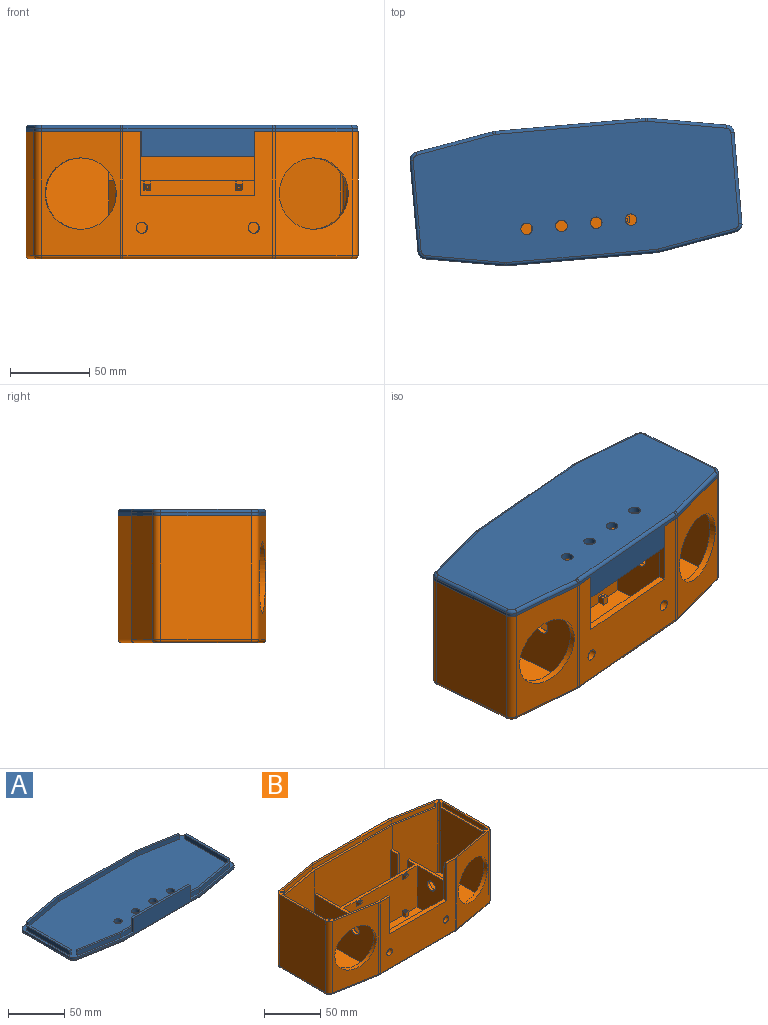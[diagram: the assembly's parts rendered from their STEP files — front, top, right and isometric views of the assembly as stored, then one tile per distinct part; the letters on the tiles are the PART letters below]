
ASSEMBLY  parts=2 mates=1
PART A: 71 faces, bbox 205.8x85.1x19.9 mm
  f0: plane 205x85mm, normal (0,0,1), area 15053.5mm2, adj f1,f2,f3,f4,f5,f6,f7,f8
  f1: plane 13.31x5mm, normal (0,-1,0), area 66.5mm2, adj f0,f49,f52,f64
  f2: plane 49.24x8.68mm, normal (-0.17,0.98,0), area 100mm2, adj f0,f3,f17,f27
  f3: cylinder r=5mm len=4.92mm, axis (0,0,1), area 14mm2, adj f0,f2,f4,f25
  f4: plane 57.48x2mm, normal (-1,0,0), area 115mm2, adj f0,f3,f5,f23
  f5: cylinder r=5mm len=4.92mm, axis (0,0,1), area 14mm2, adj f0,f4,f6,f21
  f6: plane 49.24x8.68mm, normal (-0.17,-0.98,0), area 100mm2, adj f0,f5,f7,f19
  f7: cylinder r=10mm len=2mm, axis (0,0,1), area 3.5mm2, adj f0,f6,f8,f20
  f8: plane 94.78x17.9mm, normal (0,-1,0), area 1332.8mm2, adj f0,f7,f9,f22,f64,f65,f66
  f9: cylinder r=10mm len=2mm, axis (0,0,1), area 3.5mm2, adj f0,f8,f10,f24
  f10: plane 49.24x8.68mm, normal (0.17,-0.98,0), area 100mm2, adj f0,f9,f11,f26
  f11: cylinder r=5mm len=4.92mm, axis (0,0,1), area 14mm2, adj f0,f10,f12,f28
  f12: plane 57.48x2mm, normal (1,0,0), area 115mm2, adj f0,f11,f13,f30
  f13: cylinder r=5mm len=4.92mm, axis (0,0,1), area 14mm2, adj f0,f12,f14,f32
  f14: plane 49.24x8.68mm, normal (0.17,0.98,0), area 100mm2, adj f0,f13,f15,f34
  f15: cylinder r=10mm len=2mm, axis (0,0,1), area 3.5mm2, adj f0,f14,f16,f33
  f16: plane 94.78x2mm, normal (0,1,0), area 189.6mm2, adj f0,f15,f17,f31
  f17: cylinder r=10mm len=2mm, axis (0,0,1), area 3.5mm2, adj f0,f2,f16,f29
  f18: plane 201x81mm, normal (0,0,-1), area 15139.7mm2, adj f19,f20,f21,f22,f23,f24,f25,f26
  f19: cylinder r=2mm len=49.59mm, axis (-0.98,0.17,0), area 157.1mm2, adj f6,f18,f20,f21
  f20: torus R=8mm, axis (0,0,1), area 5.1mm2, adj f7,f18,f19,f22
  f21: torus R=3mm, axis (0,0,1), area 18.7mm2, adj f5,f18,f19,f23
  f22: cylinder r=2mm len=94.78mm, axis (-1,0,0), area 297.8mm2, adj f8,f18,f20,f24
  f23: cylinder r=2mm len=57.48mm, axis (0,1,0), area 180.6mm2, adj f4,f18,f21,f25
  f24: torus R=8mm, axis (0,0,1), area 5.1mm2, adj f9,f18,f22,f26
  f25: torus R=3mm, axis (0,0,1), area 18.7mm2, adj f3,f18,f23,f27
  f26: cylinder r=2mm len=49.59mm, axis (-0.98,-0.17,0), area 157.1mm2, adj f10,f18,f24,f28
  f27: cylinder r=2mm len=49.59mm, axis (0.98,0.17,0), area 157.1mm2, adj f2,f18,f25,f29
  f28: torus R=3mm, axis (0,0,1), area 18.7mm2, adj f11,f18,f26,f30
  f29: torus R=8mm, axis (0,0,1), area 5.1mm2, adj f17,f18,f27,f31
  f30: cylinder r=2mm len=57.48mm, axis (0,-1,0), area 180.6mm2, adj f12,f18,f28,f32
  f31: cylinder r=2mm len=94.78mm, axis (1,0,0), area 297.8mm2, adj f16,f18,f29,f33
  f32: torus R=3mm, axis (0,0,1), area 18.7mm2, adj f13,f18,f30,f34
  f33: torus R=8mm, axis (0,0,1), area 5.1mm2, adj f15,f18,f31,f34
  f34: cylinder r=2mm len=49.59mm, axis (0.98,-0.17,0), area 157.1mm2, adj f14,f18,f32,f33
  f35: plane 46.56x8.21mm, normal (0.17,0.98,0), area 236.4mm2, adj f0,f36,f42,f43
  f36: plane 98.52x5mm, normal (0,1,0), area 492.6mm2, adj f0,f35,f37,f43
  f37: plane 46.56x8.21mm, normal (-0.17,0.98,0), area 236.4mm2, adj f0,f36,f38,f43
  f38: plane 5x1.97mm, normal (-0.98,-0.17,0), area 10mm2, adj f0,f37,f39,f43
  f39: plane 46.22x8.15mm, normal (0.17,-0.98,0), area 234.7mm2, adj f0,f38,f40,f43
  f40: plane 98.52x5mm, normal (0,-1,0), area 492.6mm2, adj f0,f39,f41,f43
  f41: plane 46.22x8.15mm, normal (-0.17,-0.98,0), area 234.7mm2, adj f0,f40,f42,f43
  f42: plane 5x1.97mm, normal (0.98,-0.17,0), area 10mm2, adj f0,f35,f41,f43
  f43: plane 191.65x10.18mm, normal (0,0,1), area 388.5mm2, adj f35,f36,f37,f38,f39,f40,f41,f42
  f44: plane 98.52x5mm, normal (0,1,0), area 492.6mm2, adj f0,f45,f51,f52
  f45: plane 46.22x8.15mm, normal (0.17,0.98,0), area 234.7mm2, adj f0,f44,f46,f52
  f46: plane 5x1.97mm, normal (-0.98,0.17,0), area 10mm2, adj f0,f45,f47,f52
  f47: plane 46.56x8.21mm, normal (-0.17,-0.98,0), area 236.4mm2, adj f0,f46,f48,f52
  f48: plane 13.31x5mm, normal (0,-1,0), area 66.5mm2, adj f0,f47,f52,f65
  f49: plane 46.56x8.21mm, normal (0.17,-0.98,0), area 236.4mm2, adj f0,f1,f50,f52
  f50: plane 5x1.97mm, normal (0.98,0.17,0), area 10mm2, adj f0,f49,f51,f52
  f51: plane 46.22x8.15mm, normal (-0.17,0.98,0), area 234.7mm2, adj f0,f44,f50,f52
  f52: plane 191.65x10.18mm, normal (0,0,1), area 388.5mm2, adj f1,f44,f45,f46,f47,f48,f49,f50
  f53: plane 54.21x5mm, normal (-1,0,0), area 271.1mm2, adj f0,f54,f56,f57
  f54: plane 5x2mm, normal (0,-1,0), area 10mm2, adj f0,f53,f55,f57
  f55: plane 54.21x5mm, normal (1,0,0), area 271.1mm2, adj f0,f54,f56,f57
  f56: plane 5x2mm, normal (0,1,0), area 10mm2, adj f0,f53,f55,f57
  f57: plane 54.21x2mm, normal (0,0,1), area 108.4mm2, adj f53,f54,f55,f56
  f58: plane 54.21x5mm, normal (1,0,0), area 271.1mm2, adj f0,f59,f61,f62
  f59: plane 5x2mm, normal (0,1,0), area 10mm2, adj f0,f58,f60,f62
  f60: plane 54.21x5mm, normal (-1,0,0), area 271.1mm2, adj f0,f59,f61,f62
  f61: plane 5x2mm, normal (0,-1,0), area 10mm2, adj f0,f58,f60,f62
  f62: plane 54.21x2mm, normal (0,0,1), area 108.4mm2, adj f58,f59,f60,f61
  f63: plane 71.9x10.9mm, normal (0,1,0), area 783.7mm2, adj f52,f64,f65,f66
  f64: plane 15.9x2.21mm, normal (1,0,0), area 35.1mm2, adj f0,f1,f8,f63,f66
  f65: plane 15.9x2.21mm, normal (-1,0,0), area 35.1mm2, adj f0,f8,f48,f63,f66
  f66: plane 71.9x2.21mm, normal (0,0,1), area 158.6mm2, adj f8,f63,f64,f65
  f67: cylinder r=3.65mm len=7.3mm, axis (0,0,-1), area 91.7mm2, adj f0,f18
  f68: cylinder r=3.65mm len=7.3mm, axis (0,0,-1), area 91.7mm2, adj f0,f18
  f69: cylinder r=3.65mm len=7.3mm, axis (0,0,-1), area 91.7mm2, adj f0,f18
  f70: cylinder r=3.65mm len=7.3mm, axis (0,0,-1), area 91.7mm2, adj f0,f18
PART B: 147 faces, bbox 206.2x85.4x80.4 mm
  f0: plane 76x47.59mm, normal (-0.17,0.98,0), area 1843.8mm2, adj f2,f3,f6,f10,f51,f55,f83,f136
  f1: plane 76x47.59mm, normal (0.17,0.98,0), area 1843.8mm2, adj f2,f3,f12,f50,f56,f79,f84,f135
  f2: plane 205x85mm, normal (0,0,1), area 995.4mm2, adj f0,f1,f4,f5,f9,f14,f15,f16
  f3: plane 98.52x71mm, normal (0,1,0), area 4091.9mm2, adj f0,f1,f6,f8,f53,f54,f57,f84
  f4: plane 94.78x78mm, normal (0,-1,0), area 4400.1mm2, adj f2,f19,f20,f33,f130,f131,f132,f133
  f5: plane 13.26x5mm, normal (0,1,0), area 66.3mm2, adj f2,f6,f82,f131
  f6: plane 59.82x10.18mm, normal (0,0,1), area 121.1mm2, adj f0,f3,f5,f82,f83,f131
  f7: plane 92.52x45mm, normal (0,-1,0), area 4075.4mm2, adj f8,f53,f54,f57,f95,f97,f98,f99
  f8: plane 92.52x43mm, normal (0,0,1), area 3914.3mm2, adj f3,f7,f53,f54,f95,f96,f97,f99
  f9: plane 76x47.59mm, normal (0.17,-0.98,0), area 3437.8mm2, adj f2,f12,f13,f49,f56,f77,f78
  f10: plane 145.26x76.53mm, normal (0,0,1), area 6216.6mm2, adj f0,f11,f13,f47,f48,f51,f52,f55
  f11: plane 93.02x45mm, normal (0,1,0), area 4185.9mm2, adj f10,f57,f58,f60
  f12: plane 76.53x49.24mm, normal (0,0,1), area 3339.4mm2, adj f1,f9,f46,f49,f50,f56
  f13: plane 98.52x71mm, normal (0,-1,0), area 6747.4mm2, adj f9,f10,f48,f57,f58,f62,f64,f78
  f14: plane 78x49.24mm, normal (-0.17,0.98,0), area 3900mm2, adj f2,f15,f28,f38
  f15: cylinder r=5mm len=78mm, axis (0,0,1), area 544.5mm2, adj f2,f14,f16,f36
  f16: plane 78x57.48mm, normal (-1,0,0), area 4483.5mm2, adj f2,f15,f17,f34
  f17: cylinder r=5mm len=78mm, axis (0,0,1), area 544.5mm2, adj f2,f16,f18,f32
  f18: plane 78x49.24mm, normal (-0.17,-0.98,0), area 2309.6mm2, adj f2,f17,f19,f30,f135
  f19: cylinder r=10mm len=78mm, axis (0,0,1), area 136.2mm2, adj f2,f4,f18,f31
  f20: cylinder r=10mm len=78mm, axis (0,0,1), area 136.2mm2, adj f2,f4,f21,f35
  f21: plane 78x49.24mm, normal (0.17,-0.98,0), area 2309.6mm2, adj f2,f20,f22,f37,f136
  f22: cylinder r=5mm len=78mm, axis (0,0,1), area 544.5mm2, adj f2,f21,f23,f39
  f23: plane 78x57.48mm, normal (1,0,0), area 4483.5mm2, adj f2,f22,f24,f41
  f24: cylinder r=5mm len=78mm, axis (0,0,1), area 544.5mm2, adj f2,f23,f25,f43
  f25: plane 78x49.24mm, normal (0.17,0.98,0), area 3821.5mm2, adj f2,f24,f26,f45,f145
  f26: cylinder r=10mm len=78mm, axis (0,0,1), area 136.2mm2, adj f2,f25,f27,f44
  f27: plane 94.78x78mm, normal (0,1,0), area 7393.1mm2, adj f2,f26,f28,f42
  f28: cylinder r=10mm len=78mm, axis (0,0,1), area 136.2mm2, adj f2,f14,f27,f40
  f29: plane 201x81mm, normal (0,0,-1), area 15307.1mm2, adj f30,f31,f32,f33,f34,f35,f36,f37
  f30: cylinder r=2mm len=49.59mm, axis (-0.98,0.17,0), area 157.1mm2, adj f18,f29,f31,f32
  f31: torus R=8mm, axis (0,0,1), area 5.1mm2, adj f19,f29,f30,f33
  f32: torus R=3mm, axis (0,0,1), area 18.7mm2, adj f17,f29,f30,f34
  f33: cylinder r=2mm len=94.78mm, axis (-1,0,0), area 297.8mm2, adj f4,f29,f31,f35
  f34: cylinder r=2mm len=57.48mm, axis (0,1,0), area 180.6mm2, adj f16,f29,f32,f36
  f35: torus R=8mm, axis (0,0,1), area 5.1mm2, adj f20,f29,f33,f37
  f36: torus R=3mm, axis (0,0,1), area 18.7mm2, adj f15,f29,f34,f38
  f37: cylinder r=2mm len=49.59mm, axis (-0.98,-0.17,0), area 157.1mm2, adj f21,f29,f35,f39
  f38: cylinder r=2mm len=49.59mm, axis (0.98,0.17,0), area 157.1mm2, adj f14,f29,f36,f40
  f39: torus R=3mm, axis (0,0,1), area 18.7mm2, adj f22,f29,f37,f41
  f40: torus R=8mm, axis (0,0,1), area 5.1mm2, adj f28,f29,f38,f42
  f41: cylinder r=2mm len=57.48mm, axis (0,-1,0), area 180.6mm2, adj f23,f29,f39,f43
  f42: cylinder r=2mm len=94.78mm, axis (1,0,0), area 297.8mm2, adj f27,f29,f40,f44
  f43: torus R=3mm, axis (0,0,1), area 18.7mm2, adj f24,f29,f41,f45
  f44: torus R=8mm, axis (0,0,1), area 5.1mm2, adj f26,f29,f42,f45
  f45: cylinder r=2mm len=49.59mm, axis (0.98,-0.17,0), area 157.1mm2, adj f25,f29,f43,f44
  f46: plane 76x55.8mm, normal (1,0,0), area 3969.9mm2, adj f2,f12,f49,f50,f70,f71,f72
  f47: plane 76x55.8mm, normal (-1,0,0), area 3969.9mm2, adj f2,f10,f51,f52,f65,f67,f68
  f48: plane 76x47.59mm, normal (-0.17,-0.98,0), area 3359.3mm2, adj f2,f10,f13,f52,f61,f73,f78,f145
  f49: cylinder r=2mm len=76mm, axis (0,0,1), area 212.2mm2, adj f2,f9,f12,f46
  f50: cylinder r=2mm len=76mm, axis (0,0,-1), area 212.2mm2, adj f1,f2,f12,f46
  f51: cylinder r=2mm len=76mm, axis (0,0,1), area 212.2mm2, adj f0,f2,f10,f47
  f52: cylinder r=2mm len=76mm, axis (0,0,-1), area 212.2mm2, adj f2,f10,f47,f48
  f53: plane 45x43mm, normal (1,0,0), area 1856.5mm2, adj f3,f7,f8,f57,f93
  f54: plane 45x43mm, normal (-1,0,0), area 1856.5mm2, adj f3,f7,f8,f57,f94
  f55: plane 55x45mm, normal (1,0,0), area 2396.5mm2, adj f0,f10,f57,f59,f94
  f56: plane 76.53x45mm, normal (-1,0,0), area 3365.1mm2, adj f1,f9,f12,f57,f93
  f57: plane 98.52x76.53mm, normal (0,0,1), area 684.3mm2, adj f3,f7,f11,f13,f53,f54,f55,f56
  f58: plane 45x30.53mm, normal (1,0,0), area 1373.7mm2, adj f10,f11,f13,f57
  f59: plane 45x3mm, normal (0,1,0), area 135mm2, adj f10,f55,f57,f60
  f60: plane 45x9mm, normal (-1,0,0), area 405mm2, adj f10,f11,f57,f59
  f61: plane 45x9mm, normal (1,0,0), area 405mm2, adj f10,f48,f63,f64
  f62: plane 45x9mm, normal (-1,0,0), area 405mm2, adj f10,f13,f63,f64
  f63: plane 45x3mm, normal (0,-1,0), area 135mm2, adj f10,f61,f62,f64
  f64: plane 9x3mm, normal (0,0,1), area 27mm2, adj f13,f61,f62,f63
  f65: plane 5x2mm, normal (0,1,0), area 10mm2, adj f2,f47,f66,f68
  f66: plane 54.21x5mm, normal (-1,0,0), area 271.1mm2, adj f2,f65,f67,f68
  f67: plane 5x2mm, normal (0,-1,0), area 10mm2, adj f2,f47,f66,f68
  f68: plane 54.21x2mm, normal (0,0,1), area 108.4mm2, adj f47,f65,f66,f67
  f69: plane 54.21x5mm, normal (1,0,0), area 271.1mm2, adj f2,f70,f71,f72
  f70: plane 5x2mm, normal (0,1,0), area 10mm2, adj f2,f46,f69,f72
  f71: plane 5x2mm, normal (0,-1,0), area 10mm2, adj f2,f46,f69,f72
  f72: plane 54.21x2mm, normal (0,0,1), area 108.4mm2, adj f46,f69,f70,f71
  f73: plane 5x1.97mm, normal (-0.98,0.17,0), area 10mm2, adj f2,f48,f74,f78
  f74: plane 46.56x8.21mm, normal (-0.17,-0.98,0), area 236.4mm2, adj f2,f73,f75,f78
  f75: plane 98.52x5mm, normal (0,-1,0), area 492.6mm2, adj f2,f74,f76,f78
  f76: plane 46.56x8.21mm, normal (0.17,-0.98,0), area 236.4mm2, adj f2,f75,f77,f78
  f77: plane 5x1.97mm, normal (0.98,0.17,0), area 10mm2, adj f2,f9,f76,f78
  f78: plane 191.65x10.18mm, normal (0,0,1), area 388.5mm2, adj f9,f13,f48,f73,f74,f75,f76,f77
  f79: plane 5x1.97mm, normal (0.98,-0.17,0), area 10mm2, adj f1,f2,f80,f84
  f80: plane 46.56x8.21mm, normal (0.17,0.98,0), area 236.4mm2, adj f2,f79,f81,f84
  f81: plane 13.26x5mm, normal (0,1,0), area 66.3mm2, adj f2,f80,f84,f132
  f82: plane 46.56x8.21mm, normal (-0.17,0.98,0), area 236.4mm2, adj f2,f5,f6,f83
  f83: plane 5x1.97mm, normal (-0.98,-0.17,0), area 10mm2, adj f0,f2,f6,f82
  f84: plane 59.82x10.18mm, normal (0,0,1), area 121.1mm2, adj f1,f3,f79,f80,f81,f132
  f85: cone r=0mm half-angle=59deg, axis (0,0,1), area 2.1mm2, adj f86
  f86: cylinder r=0.75mm len=20mm, axis (0,0,1), area 94.2mm2, adj f2,f85
  f87: cone r=0mm half-angle=59deg, axis (0,0,1), area 2.1mm2, adj f88
  f88: cylinder r=0.75mm len=20mm, axis (0,0,1), area 94.2mm2, adj f2,f87
  f89: cone r=0mm half-angle=59deg, axis (0,0,1), area 2.1mm2, adj f90
  f90: cylinder r=0.75mm len=20mm, axis (0,0,1), area 94.2mm2, adj f2,f89
  f91: cone r=0mm half-angle=59deg, axis (0,0,1), area 2.1mm2, adj f92
  f92: cylinder r=0.75mm len=20mm, axis (0,0,1), area 94.2mm2, adj f2,f91
  f93: cylinder r=5mm len=10mm, axis (1,0,0), area 94.2mm2, adj f53,f56
  f94: cylinder r=5mm len=10mm, axis (1,0,0), area 94.2mm2, adj f54,f55
  f95: plane 5x4mm, normal (-1,0,0), area 20mm2, adj f7,f8,f96,f98
  f96: plane 5x4mm, normal (0,-1,0), area 20mm2, adj f8,f95,f97,f98
  f97: plane 5x4mm, normal (1,0,0), area 20mm2, adj f7,f8,f96,f98
  f98: plane 4x4mm, normal (0,0,1), area 13.7mm2, adj f7,f95,f96,f97,f120
  f99: plane 5x4mm, normal (-1,0,0), area 20mm2, adj f7,f8,f100,f102
  f100: plane 5x4mm, normal (0,-1,0), area 20mm2, adj f8,f99,f101,f102
  f101: plane 5x4mm, normal (1,0,0), area 20mm2, adj f7,f8,f100,f102
  f102: plane 4x4mm, normal (0,0,1), area 13.7mm2, adj f7,f99,f100,f101,f118
  f103: plane 5x4mm, normal (0,1,0), area 20mm2, adj f8,f104,f106,f107
  f104: plane 5x4mm, normal (-1,0,0), area 20mm2, adj f8,f103,f105,f107
  f105: plane 5x4mm, normal (0,-1,0), area 20mm2, adj f8,f104,f106,f107
  f106: plane 5x4mm, normal (1,0,0), area 20mm2, adj f8,f103,f105,f107
  f107: plane 4x4mm, normal (0,0,1), area 13.7mm2, adj f103,f104,f105,f106,f116
  f108: plane 5x4mm, normal (-1,0,0), area 20mm2, adj f8,f109,f111,f112
  f109: plane 5x4mm, normal (0,-1,0), area 20mm2, adj f8,f108,f110,f112
  f110: plane 5x4mm, normal (1,0,0), area 20mm2, adj f8,f109,f111,f112
  f111: plane 5x4mm, normal (0,1,0), area 20mm2, adj f8,f108,f110,f112
  f112: plane 4x4mm, normal (0,0,1), area 13.7mm2, adj f108,f109,f110,f111,f114
  f113: plane 1.7x1.7mm, normal (0,0,1), area 2.3mm2, adj f114
  f114: cylinder r=0.85mm len=5mm, axis (0,0,-1), area 26.7mm2, adj f112,f113
  f115: plane 1.7x1.7mm, normal (0,0,1), area 2.3mm2, adj f116
  f116: cylinder r=0.85mm len=5mm, axis (0,0,-1), area 26.7mm2, adj f107,f115
  f117: plane 1.7x1.7mm, normal (0,0,1), area 2.3mm2, adj f118
  f118: cylinder r=0.85mm len=5mm, axis (0,0,-1), area 26.7mm2, adj f102,f117
  f119: plane 1.7x1.7mm, normal (0,0,1), area 2.3mm2, adj f120
  f120: cylinder r=0.85mm len=5mm, axis (0,0,-1), area 26.7mm2, adj f98,f119
  f121: plane 6x4mm, normal (-1,0,0), area 16mm2, adj f7,f57,f123,f129
  f122: plane 6x4mm, normal (1,0,0), area 16mm2, adj f7,f57,f123,f129
  f123: plane 4x2mm, normal (0,-1,0), area 8mm2, adj f57,f121,f122,f129
  f124: plane 6x4mm, normal (-1,0,0), area 16mm2, adj f7,f57,f126,f146
  f125: plane 6x4mm, normal (1,0,0), area 16mm2, adj f7,f57,f126,f146
  f126: plane 4x2mm, normal (0,-1,0), area 8mm2, adj f57,f124,f125,f146
  f127: cylinder r=0.85mm len=4.85mm, axis (0,0,1), area 21.5mm2, adj f57,f146
  f128: cylinder r=0.85mm len=4.85mm, axis (0,0,1), area 21.5mm2, adj f57,f129
  f129: plane 4.36x4.36mm, normal (0,-0.71,-0.71), area 19.4mm2, adj f7,f121,f122,f123,f128
  f130: plane 72x4.24mm, normal (0,0,1), area 305.1mm2, adj f3,f4,f131,f132
  f131: plane 40.5x4.24mm, normal (-1,0,0), area 161.4mm2, adj f2,f3,f4,f5,f6,f130
  f132: plane 40.5x4.24mm, normal (1,0,0), area 161.4mm2, adj f2,f3,f4,f81,f84,f130
  f133: cylinder r=3.5mm len=7mm, axis (0,-1,0), area 93.2mm2, adj f3,f4
  f134: cylinder r=3.5mm len=7mm, axis (0,-1,0), area 93.2mm2, adj f3,f4
  f135: cylinder r=22.5mm len=45.01mm, axis (-0.17,-0.98,0), area 565.5mm2, adj f1,f18
  f136: cylinder r=22.5mm len=45.01mm, axis (0.17,-0.98,0), area 565.5mm2, adj f0,f21
  f137: cylinder r=0.75mm len=3.22mm, axis (0.17,0.98,0), area 14.1mm2, adj f1,f138
  f138: plane 1.5x1.48mm, normal (0.17,0.98,0), area 1.8mm2, adj f137
  f139: cylinder r=0.75mm len=3.22mm, axis (0.17,0.98,0), area 14.1mm2, adj f1,f140
  f140: plane 1.5x1.48mm, normal (0.17,0.98,0), area 1.8mm2, adj f139
  f141: cylinder r=0.75mm len=3.22mm, axis (-0.17,0.98,0), area 14.1mm2, adj f0,f142
  f142: plane 1.5x1.48mm, normal (-0.17,0.98,0), area 1.8mm2, adj f141
  f143: cylinder r=0.75mm len=3.22mm, axis (-0.17,0.98,0), area 14.1mm2, adj f0,f144
  f144: plane 1.5x1.48mm, normal (-0.17,0.98,0), area 1.8mm2, adj f143
  f145: cylinder r=5mm len=10.54mm, axis (0.17,0.98,0), area 125.7mm2, adj f25,f48
  f146: plane 4.36x4.36mm, normal (0,-0.71,-0.71), area 19.4mm2, adj f7,f124,f125,f126,f127
PLACE A rot(axis=(0.04,-1,0),180deg) t=(1.5,126.82,139.96)mm
PLACE B rot(axis=(0,0,1),5deg) t=(1.5,126.82,139.96)mm
MATE fastened B.f72 <-> A.f62  axis (0,0,1) through (-97.62,118.15,134.96)mm
